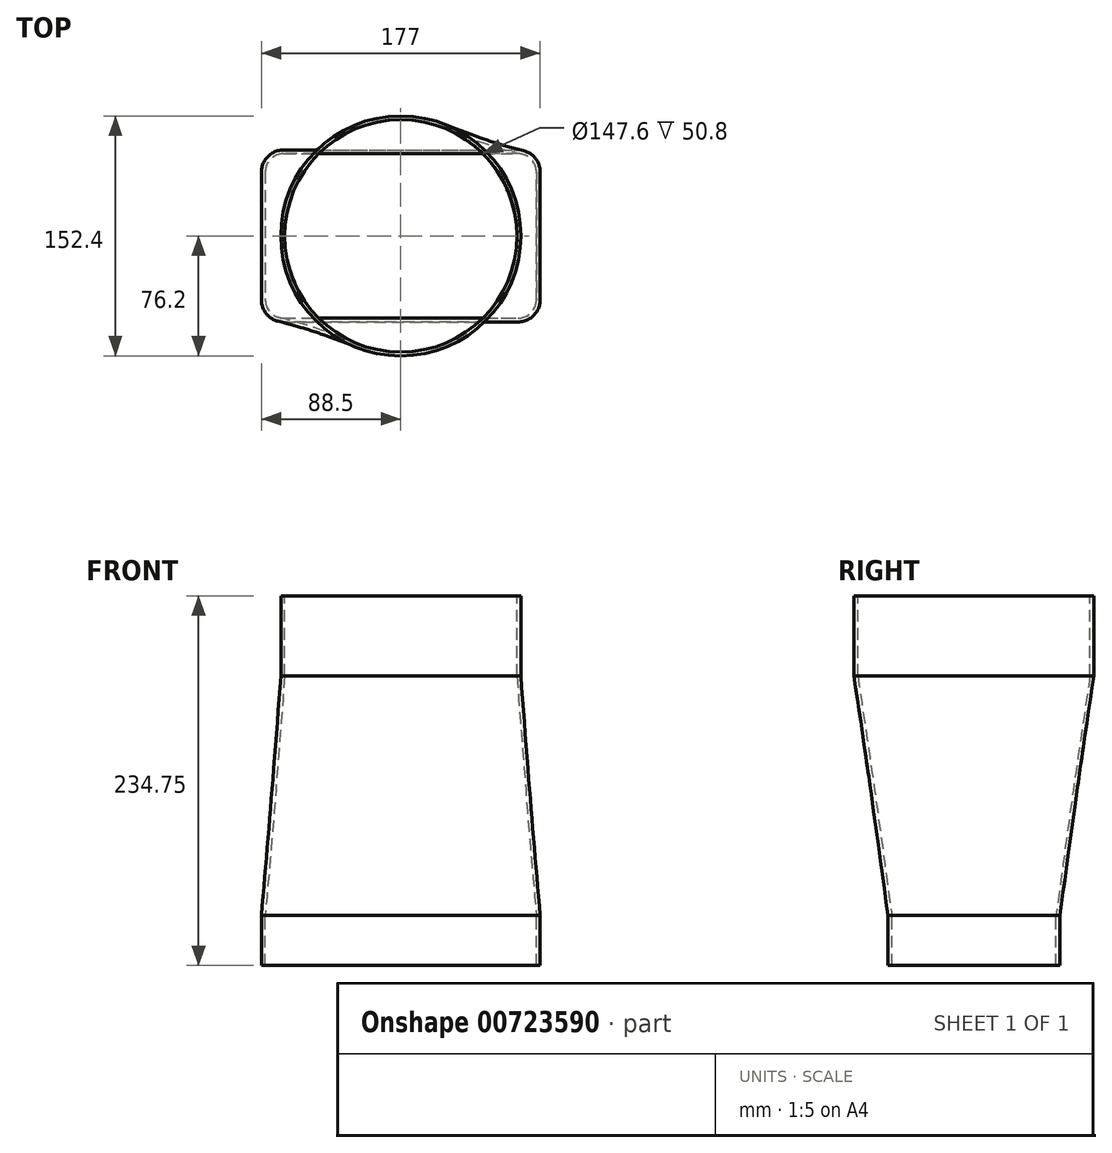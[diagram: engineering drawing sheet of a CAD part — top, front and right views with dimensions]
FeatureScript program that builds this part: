
annotation { "Feature Type Name" : "Feature", "Feature Type Description" : "" }
export const myFeature = defineFeature(function(context is Context, id is Id, definition is map)
    precondition{}
    {
        {
            var Q0;
            Q0=qCreatedBy(makeId("Top.planeOp"),FACE);
            var sketch = newSketch(context, id + "F0", { "sketchPlane" : qUnion([Q0])});
            skLineSegment(sketch, "E0.bottom", {"start": v(-74.5, 54.6) * mm, "end": v(74.5, 54.6) * mm});
            skLineSegment(sketch, "E0.top", {"start": v(-74.5, -54.6) * mm, "end": v(74.5, -54.6) * mm});
            skLineSegment(sketch, "E0.left", {"start": v(-88.5, 40.61) * mm, "end": v(-88.5, -40.6) * mm});
            skLineSegment(sketch, "E0.right", {"start": v(88.5, 40.61) * mm, "end": v(88.5, -40.6) * mm});
            skLineSegment(sketch, "E1", {"start": v(0, 0) * mm, "end": v(0, 54.6) * mm});
            skPoint(sketch, "E2.visualSharp", {"position": v(88.5, 54.6) * mm});
            skArc(sketch, "E2.filletArc", {"start": v(88.5, 40.61) * mm, "mid": v(84.4, 50.5) * mm, "end": v(74.5, 54.61) * mm});
            skPoint(sketch, "E3.visualSharp", {"position": v(88.5, -54.6) * mm});
            skArc(sketch, "E3.filletArc", {"start": v(74.5, -54.6) * mm, "mid": v(84.4, -50.5) * mm, "end": v(88.5, -40.6) * mm});
            skPoint(sketch, "E4.visualSharp", {"position": v(-88.5, -54.6) * mm});
            skArc(sketch, "E4.filletArc", {"start": v(-88.5, -40.6) * mm, "mid": v(-84.4, -50.5) * mm, "end": v(-74.5, -54.6) * mm});
            skPoint(sketch, "E5.visualSharp", {"position": v(-88.5, 54.6) * mm});
            skArc(sketch, "E5.filletArc", {"start": v(-74.5, 54.61) * mm, "mid": v(-84.4, 50.5) * mm, "end": v(-88.5, 40.61) * mm});
            skArc(sketch, "E6.0", {"start": v(-74.5, 52.21) * mm, "mid": v(-82.7, 48.81) * mm, "end": v(-86.1, 40.61) * mm});
            skLineSegment(sketch, "E6.1", {"start": v(-74.5, 52.2) * mm, "end": v(74.5, 52.2) * mm});
            skLineSegment(sketch, "E6.2", {"start": v(-86.1, 40.61) * mm, "end": v(-86.1, -40.6) * mm});
            skArc(sketch, "E6.3", {"start": v(86.1, 40.61) * mm, "mid": v(82.7, 48.81) * mm, "end": v(74.5, 52.21) * mm});
            skArc(sketch, "E6.4", {"start": v(-86.1, -40.6) * mm, "mid": v(-82.7, -48.81) * mm, "end": v(-74.5, -52.2) * mm});
            skLineSegment(sketch, "E6.5", {"start": v(-74.5, -52.2) * mm, "end": v(74.5, -52.2) * mm});
            skArc(sketch, "E6.6", {"start": v(74.5, -52.2) * mm, "mid": v(82.7, -48.81) * mm, "end": v(86.1, -40.6) * mm});
            skLineSegment(sketch, "E6.7", {"start": v(86.1, 40.61) * mm, "end": v(86.1, -40.6) * mm});
            skSolve(sketch);
        }
        {
            var Q0;
            Q0=qSketchRegion(id+"F0",true);
            var Q1;
            {var subQ3=sQuery(id+"F0.wireOp",EDGE,"E6.0");Q1=makeQuery(id+"F0.imprint","IMPRINT",FACE,{"disambiguationData":[TD([[makeQuery(id+"F0.imprint","IMPRINT",EDGE,{"derivedFrom":subQ3}),1.0]])]});}
            extrude(context, id + "F1", {"entities" : qUnion([Q0, Q1]), "oppositeDirection" : true, "depth" : 31.75 * mm, "offsetDistance" : 25.4 * mm});
        }
        {
            var Q0;
            Q0=qCreatedBy(makeId("Top.planeOp"),FACE);
            cPlane(context, id + "F2", {"entities" : qUnion([Q0]), "cplaneType" : CPlaneType.OFFSET, "offset" : 203 * mm, "width" : 152.4 * mm, "height" : 152.4 * mm});
        }
        {
            var Q0;
            Q0=qCreatedBy(id+"F2.planeOp",FACE);
            var sketch = newSketch(context, id + "F3", { "sketchPlane" : qUnion([Q0])});
            skCircle(sketch, "E7", {"center": v(0, 0) * mm, "radius": 76.2 * mm});
            skCircle(sketch, "E8", {"center": v(0, 0) * mm, "radius": 73.8 * mm});
            skSolve(sketch);
        }
        {
            var Q0;
            Q0=qSketchRegion(id+"F3",true);
            var Q1;
            Q1=makeQuery(id+"F3.imprint","IMPRINT",FACE,{"disambiguationData":[TD([[makeQuery(id+"F3.imprint","IMPRINT",EDGE,{"derivedFrom":sQuery(id+"F3.wireOp",EDGE,"E8")}),1.0]])]});
            extrude(context, id + "F4", {"entities" : qUnion([Q0, Q1]), "oppositeDirection" : true, "depth" : 50.8 * mm, "offsetDistance" : 25.4 * mm});
        }
        {
            var Q1;
            Q1=makeQuery(id+"F1.opExtrude","CAP_FACE",FACE,{"disambiguationData":[OSD([sQuery(id+"F0.wireOp",EDGE,"E0.bottom"),sQuery(id+"F0.wireOp",EDGE,"E0.top"),sQuery(id+"F0.wireOp",EDGE,"E0.left"),sQuery(id+"F0.wireOp",EDGE,"E0.right"),sQuery(id+"F0.wireOp",EDGE,"E2.filletArc"),sQuery(id+"F0.wireOp",EDGE,"E3.filletArc"),sQuery(id+"F0.wireOp",EDGE,"E4.filletArc"),sQuery(id+"F0.wireOp",EDGE,"E5.filletArc")])],"isStart":true});
            var Q2;
            Q2=makeQuery(id+"F4.opExtrude","CAP_FACE",FACE,{"disambiguationData":[OSD([sQuery(id+"F3.wireOp",EDGE,"E7")])],"isStart":false});
            loft(context, id + "F5", {"operationType" : NewBodyOperationType.ADD, "sheetProfilesArray" : [{ "sheetProfileEntities" : qUnion([Q1]) }, { "sheetProfileEntities" : qUnion([Q2]) }]});
        }
        {
            var Q0;
            Q0=makeQuery(id+"F3.imprint","IMPRINT",FACE,{"disambiguationData":[TD([[makeQuery(id+"F3.imprint","IMPRINT",EDGE,{"derivedFrom":sQuery(id+"F3.wireOp",EDGE,"E8")}),1.0]])]});
            extrude(context, id + "F6", {"entities" : qUnion([Q0]), "operationType" : NewBodyOperationType.REMOVE, "oppositeDirection" : true, "depth" : 50.8 * mm, "offsetDistance" : 25.4 * mm});
        }
        {
            var Q0;
            {var subQ3=sQuery(id+"F0.wireOp",EDGE,"E6.0");Q0=makeQuery(id+"F0.imprint","IMPRINT",FACE,{"disambiguationData":[TD([[makeQuery(id+"F0.imprint","IMPRINT",EDGE,{"derivedFrom":subQ3}),1.0]])]});}
            extrude(context, id + "F7", {"entities" : qUnion([Q0]), "operationType" : NewBodyOperationType.REMOVE, "oppositeDirection" : true, "depth" : 50.8 * mm, "offsetDistance" : 25.4 * mm});
        }
        {
            var Q1;
            Q1=makeQuery(id+"F7.boolean.opBoolean","COPY",FACE,{"derivedFrom":makeQuery(id+"F7.opExtrude","CAP_FACE",FACE,{"disambiguationData":[OSD([sQuery(id+"F0.wireOp",EDGE,"E6.0"),sQuery(id+"F0.wireOp",EDGE,"E6.1"),sQuery(id+"F0.wireOp",EDGE,"E6.2"),sQuery(id+"F0.wireOp",EDGE,"E6.3"),sQuery(id+"F0.wireOp",EDGE,"E6.4"),sQuery(id+"F0.wireOp",EDGE,"E6.5"),sQuery(id+"F0.wireOp",EDGE,"E6.6"),sQuery(id+"F0.wireOp",EDGE,"E6.7")])],"isStart":true})});
            var Q2;
            Q2=makeQuery(id+"F6.boolean.opBoolean","COPY",FACE,{"derivedFrom":makeQuery(id+"F6.opExtrude","CAP_FACE",FACE,{"disambiguationData":[OSD([sQuery(id+"F3.wireOp",EDGE,"E8")])],"isStart":false})});
            loft(context, id + "F8", {"operationType" : NewBodyOperationType.REMOVE, "sheetProfilesArray" : [{ "sheetProfileEntities" : qUnion([Q1]) }, { "sheetProfileEntities" : qUnion([Q2]) }]});
        }
    });
